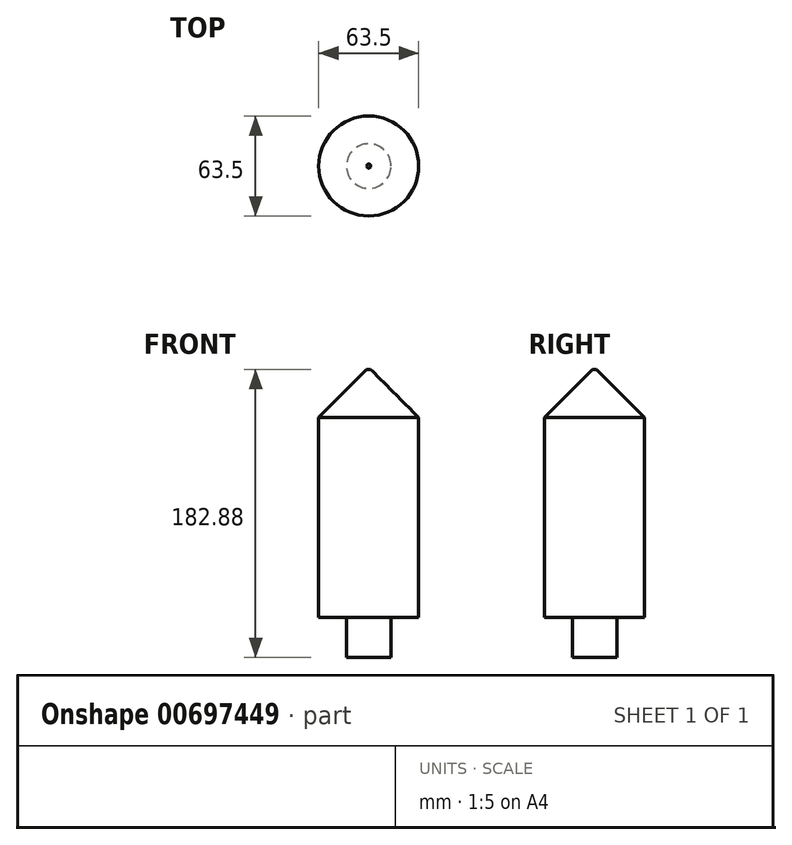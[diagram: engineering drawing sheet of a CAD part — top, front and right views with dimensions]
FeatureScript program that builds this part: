
annotation { "Feature Type Name" : "Feature", "Feature Type Description" : "" }
export const myFeature = defineFeature(function(context is Context, id is Id, definition is map)
    precondition{}
    {
        {
            var Q0;
            Q0=qCreatedBy(makeId("Top.planeOp"),FACE);
            var sketch = newSketch(context, id + "F0", { "sketchPlane" : qUnion([Q0])});
            skCircle(sketch, "E0", {"center": v(0, 0) * mm, "radius": 31.75 * mm});
            skSolve(sketch);
        }
        {
            var Q0;
            Q0 = qSketchRegion(id + "F0", true);
            extrude(context, id + "F1", {"entities" : qUnion([Q0]), "depth" : 127 * mm, "offsetDistance" : 25.4 * mm});
        }
        {
            var Q0;
            Q0=makeQuery(id+"F1.opExtrude","CAP_FACE",FACE,{"disambiguationData":[OSD([sQuery(id+"F0.wireOp",EDGE,"E0")])],"isStart":false});
            var sketch = newSketch(context, id + "F2", { "sketchPlane" : qUnion([Q0])});
            skCircle(sketch, "E1", {"center": v(0, 0) * mm, "radius": 31.75 * mm});
            skSolve(sketch);
        }
        {
            var Q0;
            Q0 = qSketchRegion(id + "F2", true);
            extrude(context, id + "F3", {"entities" : qUnion([Q0]), "operationType" : NewBodyOperationType.ADD, "depth" : 30.48 * mm, "offsetDistance" : 25.4 * mm});
        }
        {
            var Q0;
            Q0=makeQuery(id+"F3.opExtrude","CAP_EDGE",EDGE,{"disambiguationData":[OSD([sQuery(id+"F2.wireOp",EDGE,"E1")])],"isStart":false});
            chamfer(context, id + "F4", {"entities" : qUnion([Q0]), "width" : 30.48 * mm, "tangentPropagation" : true});
        }
        {
            var Q0;
            Q0=makeQuery(id+"F1.opExtrude","CAP_FACE",FACE,{"disambiguationData":[OSD([sQuery(id+"F0.wireOp",EDGE,"E0")])],"isStart":true});
            var sketch = newSketch(context, id + "F5", { "sketchPlane" : qUnion([Q0])});
            skCircle(sketch, "E2", {"center": v(0, 0) * mm, "radius": 14.18 * mm});
            skSolve(sketch);
        }
        {
            var Q0;
            Q0 = qSketchRegion(id + "F5", true);
            extrude(context, id + "F6", {"entities" : qUnion([Q0]), "operationType" : NewBodyOperationType.ADD, "depth" : 25.4 * mm, "offsetDistance" : 25.4 * mm});
        }
    });
